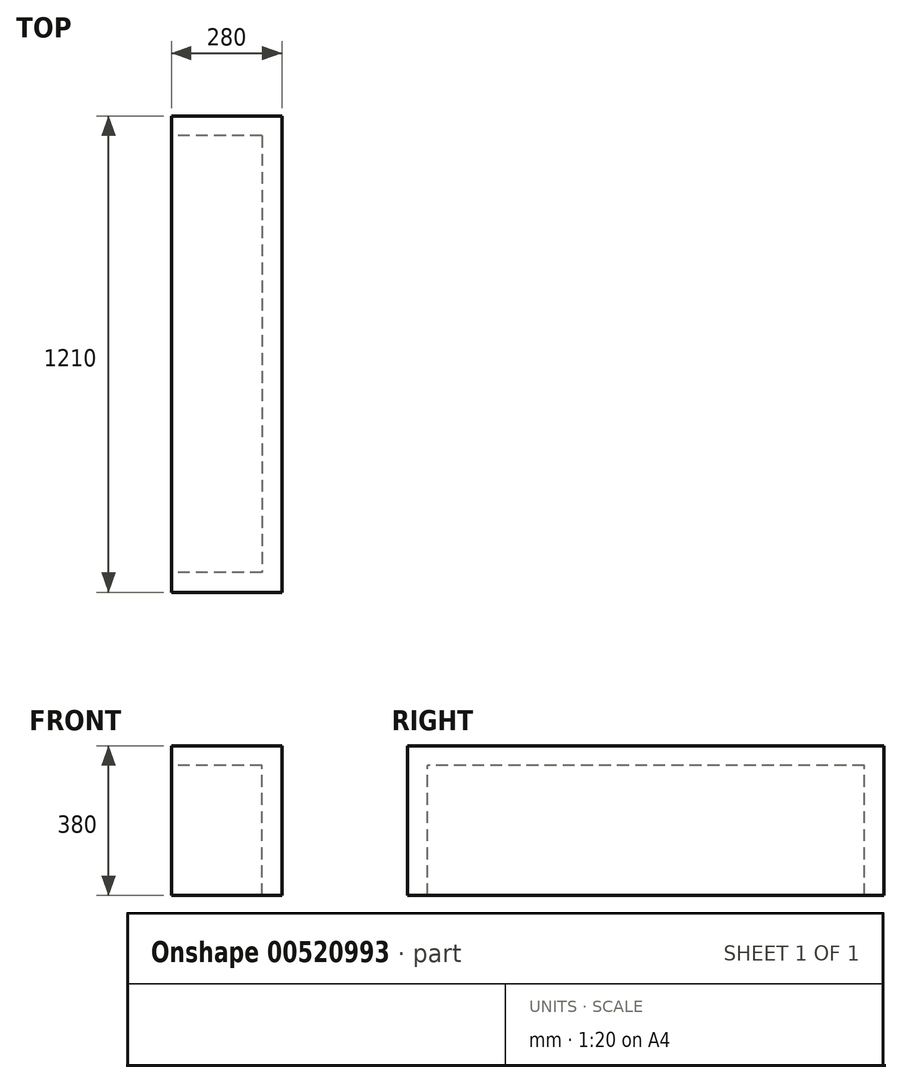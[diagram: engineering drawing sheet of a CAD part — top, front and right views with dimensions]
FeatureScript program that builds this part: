
annotation { "Feature Type Name" : "Feature", "Feature Type Description" : "" }
export const myFeature = defineFeature(function(context is Context, id is Id, definition is map)
    precondition{}
    {
        {
            var Q0;
            Q0=qCreatedBy(makeId("Right.planeOp"),FACE);
            var sketch = newSketch(context, id + "F0", { "sketchPlane" : qUnion([Q0])});
            skLineSegment(sketch, "E0.bottom", {"start": v(0, 0) * mm, "end": v(-1110, 0) * mm});
            skLineSegment(sketch, "E1.0", {"start": v(-1160, 0) * mm, "end": v(-1160, 380) * mm});
            skLineSegment(sketch, "E1.2", {"start": v(50, 0) * mm, "end": v(50, 380) * mm});
            skLineSegment(sketch, "E1.3", {"start": v(50, 380) * mm, "end": v(-1160, 380) * mm});
            skLineSegment(sketch, "E2", {"start": v(-1110, 0) * mm, "end": v(-1160, 0) * mm});
            skLineSegment(sketch, "E3", {"start": v(0, 0) * mm, "end": v(50, 0) * mm});
            skSolve(sketch);
        }
        {
            var Q0;
            Q0 = qSketchRegion(id + "F0", true);
            extrude(context, id + "F1", {"entities" : qUnion([Q0]), "depth" : 280 * mm, "offsetDistance" : 25 * mm});
        }
        {
            var Q0;
            Q0=makeQuery(id+"F1.opExtrude","CAP_FACE",FACE,{"disambiguationData":[OSD([sQuery(id+"F0.wireOp",EDGE,"E0.bottom"),sQuery(id+"F0.wireOp",EDGE,"E1.0"),sQuery(id+"F0.wireOp",EDGE,"E1.2"),sQuery(id+"F0.wireOp",EDGE,"E1.3"),sQuery(id+"F0.wireOp",EDGE,"E2"),sQuery(id+"F0.wireOp",EDGE,"E3")])],"isStart":true});
            var Q1;
            Q1=makeQuery(id+"F1.opExtrude","SWEPT_FACE",FACE,{"disambiguationData":[OSD([sQuery(id+"F0.wireOp",EDGE,"E0.bottom"),sQuery(id+"F0.wireOp",EDGE,"E2"),sQuery(id+"F0.wireOp",EDGE,"E3")])]});
            shell(context, id + "F2", {"entities" : qUnion([Q0, Q1]), "thickness" : 50 * mm});
        }
    });
